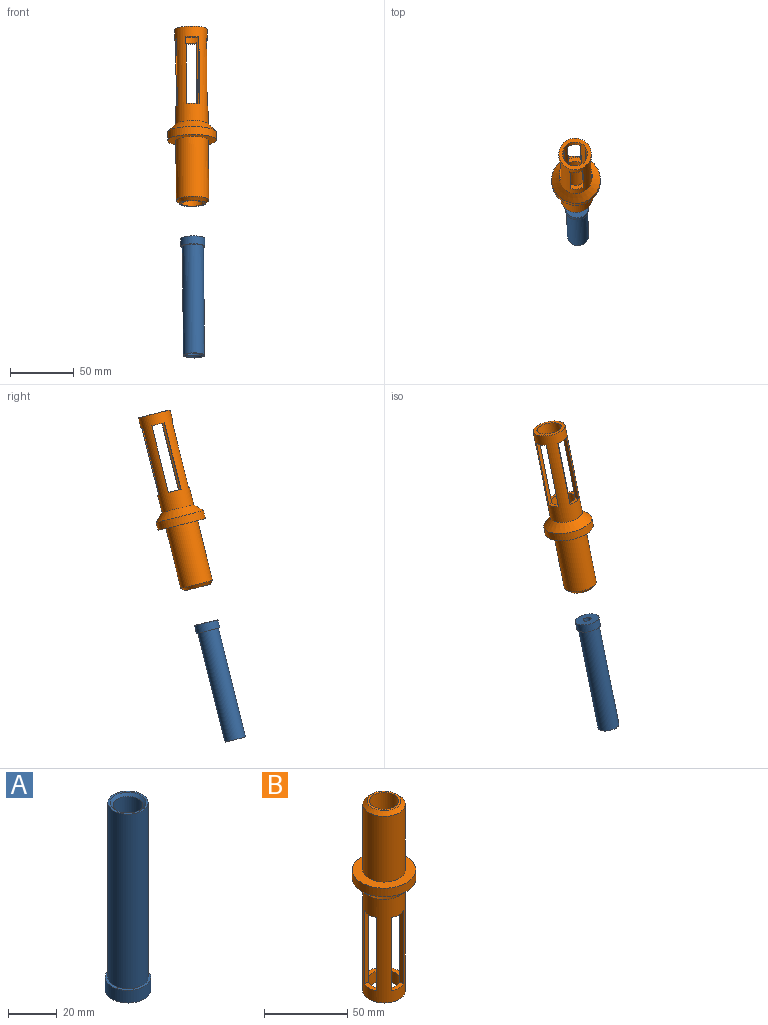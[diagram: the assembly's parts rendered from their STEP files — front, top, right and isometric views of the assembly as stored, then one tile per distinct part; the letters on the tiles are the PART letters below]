
ASSEMBLY  parts=2 mates=1
PART A: 9 faces, bbox 18.8x18.8x94 mm
  f0: plane 12.19x12.19mm, normal (0,0,1), area 85.1mm2, adj f4,f7
  f1: cylinder r=9.4mm len=18.8mm, axis (0,0,1), area 375mm2, adj f2,f3
  f2: plane 18.8x18.8mm, normal (0,0,-1), area 245.8mm2, adj f1,f4
  f3: plane 18.8x18.8mm, normal (0,0,1), area 63.4mm2, adj f1,f5
  f4: cylinder r=3.17mm len=6.35mm, axis (0,0,1), area 126.7mm2, adj f0,f2
  f5: cylinder r=8.26mm len=87.63mm, axis (0,0,-1), area 4545.2mm2, adj f3,f6
  f6: plane 16.51x16.51mm, normal (0,0,1), area 43.6mm2, adj f5,f8
  f7: cylinder r=6.1mm len=86.36mm, axis (0,0,-1), area 3307.8mm2, adj f0,f8
  f8: cone r=7.37mm half-angle=45deg, axis (0,0,1), area 76mm2, adj f6,f7
PART B: 27 faces, bbox 38.1x38.1x139.7 mm
  f0: cylinder r=12.7mm len=76.2mm, axis (0,0,1), area 3829.1mm2, adj f9,f10,f11,f12,f13,f14,f15,f16
  f1: cylinder r=9.65mm len=76.2mm, axis (0,0,1), area 2316.6mm2, adj f2,f9,f11,f12,f13,f14,f15,f16
  f2: plane 19.3x19.3mm, normal (0,0,-1), area 51.4mm2, adj f1,f5
  f3: cylinder r=12.7mm len=48.26mm, axis (0,0,-1), area 3851mm2, adj f6,f8
  f4: plane 20.32x20.32mm, normal (0,0,1), area 83mm2, adj f5,f6
  f5: cylinder r=8.76mm len=63.5mm, axis (0,0,-1), area 3496.3mm2, adj f2,f4
  f6: cone r=10.16mm half-angle=45deg, axis (0,0,-1), area 258mm2, adj f3,f4
  f7: cylinder r=19.05mm len=38.1mm, axis (0,0,-1), area 760.1mm2, adj f8,f10
  f8: plane 38.1x38.1mm, normal (0,0,1), area 633.4mm2, adj f3,f7
  f9: plane 25.4x25.4mm, normal (0,0,-1), area 214mm2, adj f0,f1
  f10: cone r=19.05mm half-angle=45deg, axis (0,0,1), area 895.7mm2, adj f0,f7
  f11: plane 53.85x3.43mm, normal (0,1,0), area 184.8mm2, adj f0,f1,f13,f14
  f12: plane 53.85x3.43mm, normal (0,-1,0), area 184.8mm2, adj f0,f1,f13,f14
  f13: plane 10.16x4.49mm, normal (0,0,-1), area 32.2mm2, adj f0,f1,f11,f12
  f14: plane 10.16x4.49mm, normal (0,0,1), area 32.2mm2, adj f0,f1,f11,f12
  f15: plane 53.85x3.43mm, normal (0,-1,0), area 184.8mm2, adj f0,f1,f17,f18
  f16: plane 53.85x3.43mm, normal (0,1,0), area 184.8mm2, adj f0,f1,f17,f18
  f17: plane 10.16x4.49mm, normal (0,0,-1), area 32.2mm2, adj f0,f1,f15,f16
  f18: plane 10.16x4.49mm, normal (0,0,1), area 32.2mm2, adj f0,f1,f15,f16
  f19: plane 10.16x4.49mm, normal (0,0,1), area 32.2mm2, adj f0,f1,f21,f22
  f20: plane 10.16x4.49mm, normal (0,0,-1), area 32.2mm2, adj f0,f1,f21,f22
  f21: plane 53.85x3.43mm, normal (1,0,0), area 184.8mm2, adj f0,f1,f19,f20
  f22: plane 53.85x3.43mm, normal (-1,0,0), area 184.8mm2, adj f0,f1,f19,f20
  f23: plane 10.16x4.49mm, normal (0,0,1), area 32.2mm2, adj f0,f1,f25,f26
  f24: plane 10.16x4.49mm, normal (0,0,-1), area 32.2mm2, adj f0,f1,f25,f26
  f25: plane 53.85x3.43mm, normal (-1,0,0), area 184.8mm2, adj f0,f1,f23,f24
  f26: plane 53.85x3.43mm, normal (1,0,0), area 184.8mm2, adj f0,f1,f23,f24
PLACE A rot(axis=(1,0.1,-0.01),166deg) t=(74.29,-33.14,-198.99)mm
PLACE B rot(axis=(0.73,-0.67,0.09),170.1deg) t=(73.43,-9.42,-103.64)mm
MATE cylindrical B.f0 <-> A.f1  axis (0.01,-0.24,-0.97) through (73.09,-0.23,-66.67)mm
